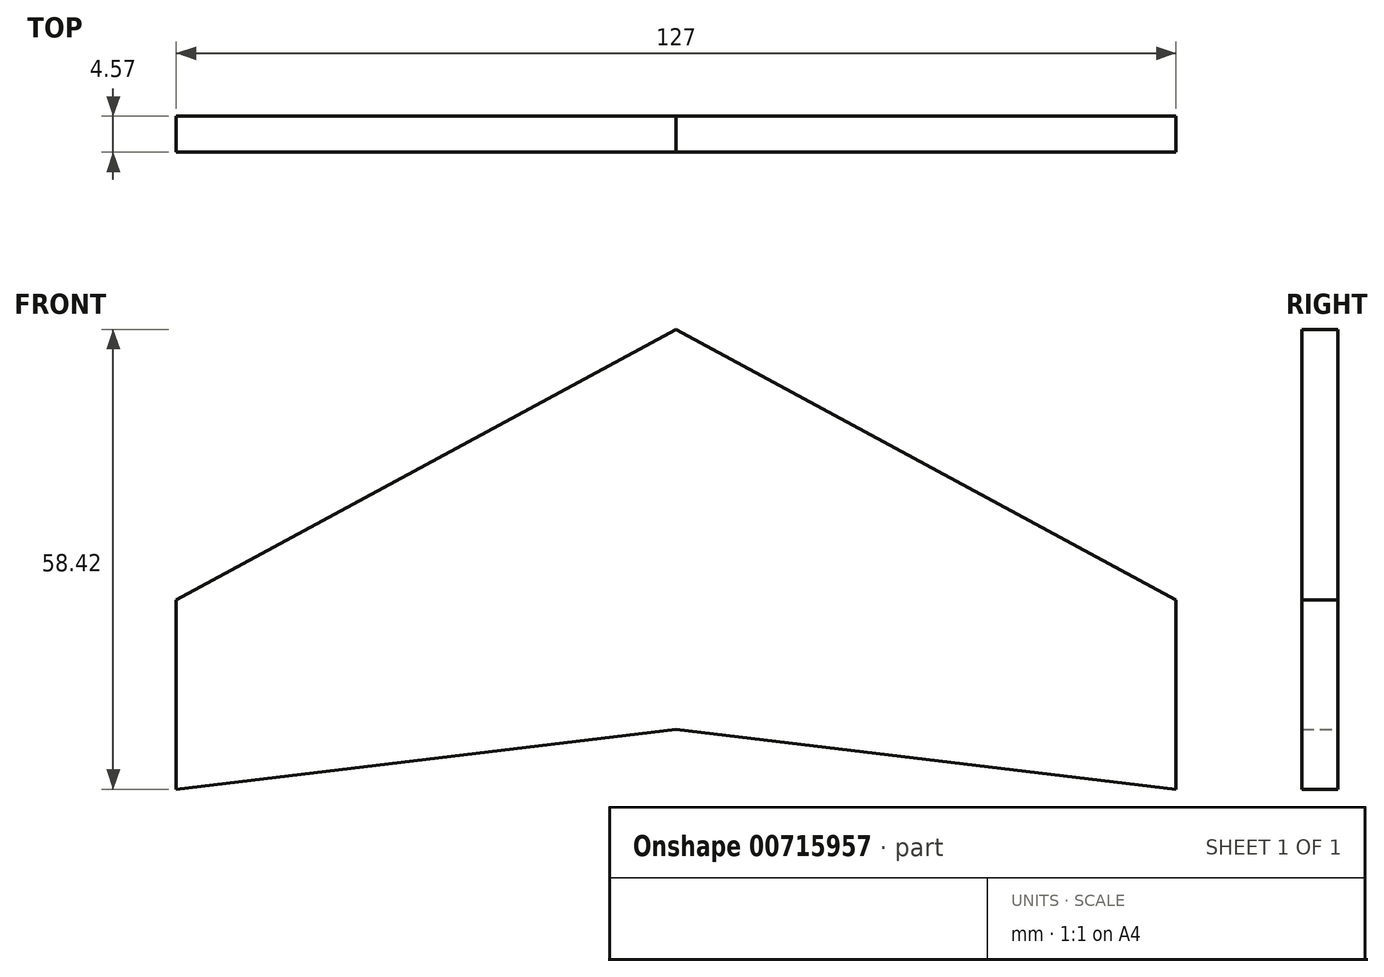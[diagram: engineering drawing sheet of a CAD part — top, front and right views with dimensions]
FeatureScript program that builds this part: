
annotation { "Feature Type Name" : "Feature", "Feature Type Description" : "" }
export const myFeature = defineFeature(function(context is Context, id is Id, definition is map)
    precondition{}
    {
        {
            var Q0;
            Q0=qCreatedBy(makeId("Front.planeOp"),FACE);
            var sketch = newSketch(context, id + "F0", { "sketchPlane" : qUnion([Q0])});
            skLineSegment(sketch, "E0.bottom", {"start": v(0, 0) * mm, "end": v(127, 0) * mm});
            skLineSegment(sketch, "E0.top", {"start": v(0, 58.42) * mm, "end": v(127, 58.42) * mm});
            skLineSegment(sketch, "E0.left", {"start": v(0, 0) * mm, "end": v(0, 58.42) * mm});
            skLineSegment(sketch, "E0.right", {"start": v(127, 0) * mm, "end": v(127, 58.42) * mm});
            skLineSegment(sketch, "E1", {"start": v(63.5, 58.42) * mm, "end": v(63.5, 0) * mm});
            skLineSegment(sketch, "E2", {"start": v(0, 7.62) * mm, "end": v(127, 7.62) * mm});
            skLineSegment(sketch, "E3", {"start": v(0, 0) * mm, "end": v(63.5, 7.62) * mm});
            skLineSegment(sketch, "E4", {"start": v(0, 0) * mm, "end": v(0, 24.07) * mm});
            skLineSegment(sketch, "E5", {"start": v(0, 24.07) * mm, "end": v(63.5, 58.42) * mm});
            skLineSegment(sketch, "E6.MirrorCS", {"start": v(127, 24.07) * mm, "end": v(63.5, 58.42) * mm});
            skLineSegment(sketch, "E7.MirrorCS", {"start": v(127, 0) * mm, "end": v(127, 24.07) * mm});
            skLineSegment(sketch, "E8.MirrorCS", {"start": v(127, 0) * mm, "end": v(63.5, 7.62) * mm});
            skSolve(sketch);
        }
        {
            var Q0;
            {var subQ0=sQuery(id+"F0.wireOp",EDGE,"E5");Q0=makeQuery(id+"F0.imprint","IMPRINT",FACE,{"disambiguationData":[TD([[makeQuery(id+"F0.imprint","IMPRINT",EDGE,{"derivedFrom":subQ0}),-1.0]])]});}
            var Q1;
            {var subQ3=sQuery(id+"F0.wireOp",EDGE,"E3");Q1=makeQuery(id+"F0.imprint","IMPRINT",FACE,{"disambiguationData":[TD([[makeQuery(id+"F0.imprint","IMPRINT",EDGE,{"derivedFrom":subQ3}),1.0]])]});}
            var Q2;
            {var subQ0=sQuery(id+"F0.wireOp",EDGE,"E6.MirrorCS");Q2=makeQuery(id+"F0.imprint","IMPRINT",FACE,{"disambiguationData":[TD([[makeQuery(id+"F0.imprint","IMPRINT",EDGE,{"derivedFrom":subQ0}),1.0]])]});}
            var Q3;
            {var subQ3=sQuery(id+"F0.wireOp",EDGE,"E8.MirrorCS");Q3=makeQuery(id+"F0.imprint","IMPRINT",FACE,{"disambiguationData":[TD([[makeQuery(id+"F0.imprint","IMPRINT",EDGE,{"derivedFrom":subQ3}),-1.0]])]});}
            extrude(context, id + "F1", {"entities" : qUnion([Q0, Q1, Q2, Q3]), "depth" : 4.57 * mm, "offsetDistance" : 25.4 * mm});
        }
    });
